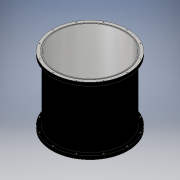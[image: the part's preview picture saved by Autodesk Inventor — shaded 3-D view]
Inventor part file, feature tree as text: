
AUTODESK INVENTOR PART (.ipt)
format: ipt  version: 2018 (Build 220112000, 112)  size: 200,192 bytes
history: native  units: in
note: dims shown in document units (in); Inventor stores cm internally (conversion verified against a paired STEP export)
features: sketch x6, extrude x4, hole x2, pattern_circular x2
ambient origin geometry x8: Origin, YZ Plane, XZ Plane, XY Plane, X Axis, Y Axis, Z Axis, Center Point
bodies: Solid1 (feature_tree)
feature tree (14):
  extrude  "Extrusion1"  Depth=19.125in
  extrude  "Extrusion2"  Depth=1.0in
  hole  "Hole1"  [1 undecoded]
  pattern_circular  "Circular Pattern1"  Count=12 Angle=360.0deg
  extrude  "Extrusion3"  Depth=1.0in
  sketch  "Sketch1"  dims[d0=21.5in d1=19.125in]
  sketch  "Sketch2"  dims[d2=1.0in d3=0.0in d4=19.5in]
  sketch  "Sketch3"  dims[d5=19.875in d6=0.125in d7=0.0in]
  sketch  "Sketch4"  dims[d8=10.4429in]
  sketch  "Sketch7"  dims[d19=19.125in d20=19.375in d21=17.0in d22=0.0in d23=19.125in d24=21.5in d26=0.0in d27=1.0in d33=0.551in d34=10.4429in d35=0.8108in d36=0.5635in d37=0.25in d38=0.375in d39=0.708in d40=0.354in d41=360.0deg d43=4.7244in]
  sketch  "Sketch5"  dims[d9=0.244in d10=0.551in d11=0.375in d12=0.25in d13=0.5635in d14=0.708in d15=0.8108in d16=4.7244in d17=360.0deg]
  extrude  "Extrusion4"  Depth=17.0in TaperAngle=0.0deg
  pattern_circular  "Circular Pattern2"  [2 undecoded]
  hole  "Hole2"  [1 undecoded]
note: 4 required parameter values undecoded (feature->parameter linkage not recoverable at this tier; creation-order binding heuristic only, values carry confidence <= 0.55)
